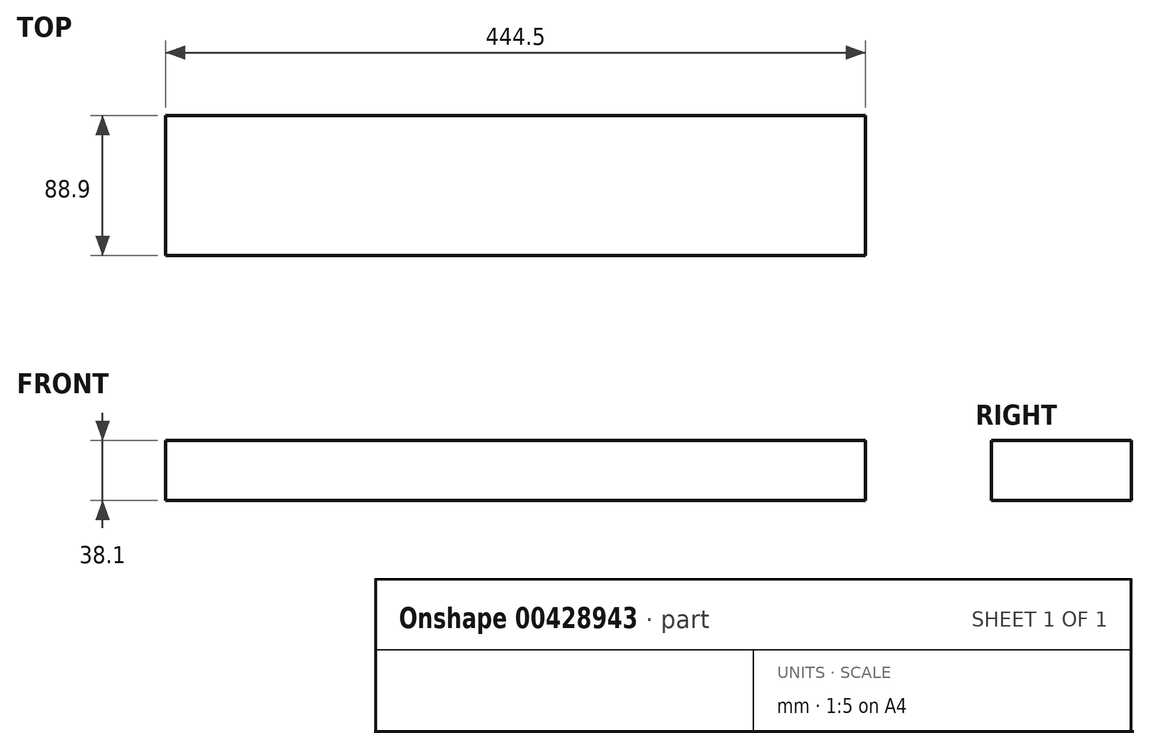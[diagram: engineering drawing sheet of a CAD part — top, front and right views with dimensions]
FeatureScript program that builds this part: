
annotation { "Feature Type Name" : "Feature", "Feature Type Description" : "" }
export const myFeature = defineFeature(function(context is Context, id is Id, definition is map)
    precondition{}
    {
        {
            var Q0;
            Q0=qCreatedBy(makeId("Top.planeOp"),FACE);
            var sketch = newSketch(context, id + "F0", { "sketchPlane" : qUnion([Q0])});
            skLineSegment(sketch, "E0.bottom", {"start": v(-341.82, 40.41) * mm, "end": v(102.68, 40.41) * mm});
            skLineSegment(sketch, "E0.top", {"start": v(-341.82, -48.49) * mm, "end": v(102.68, -48.49) * mm});
            skLineSegment(sketch, "E0.left", {"start": v(-341.82, 40.41) * mm, "end": v(-341.82, -48.49) * mm});
            skLineSegment(sketch, "E0.right", {"start": v(102.68, 40.41) * mm, "end": v(102.68, -48.49) * mm});
            skSolve(sketch);
        }
        {
            var Q0;
            Q0=makeQuery(id+"F0.imprint","IMPRINT",FACE,{"disambiguationData":[TD([[makeQuery(id+"F0.imprint","IMPRINT",EDGE,{"derivedFrom":sQuery(id+"F0.wireOp",EDGE,"E0.bottom")}),-1.0]])]});
            extrude(context, id + "F1", {"entities" : qUnion([Q0]), "depth" : 38.1 * mm});
        }
    });
